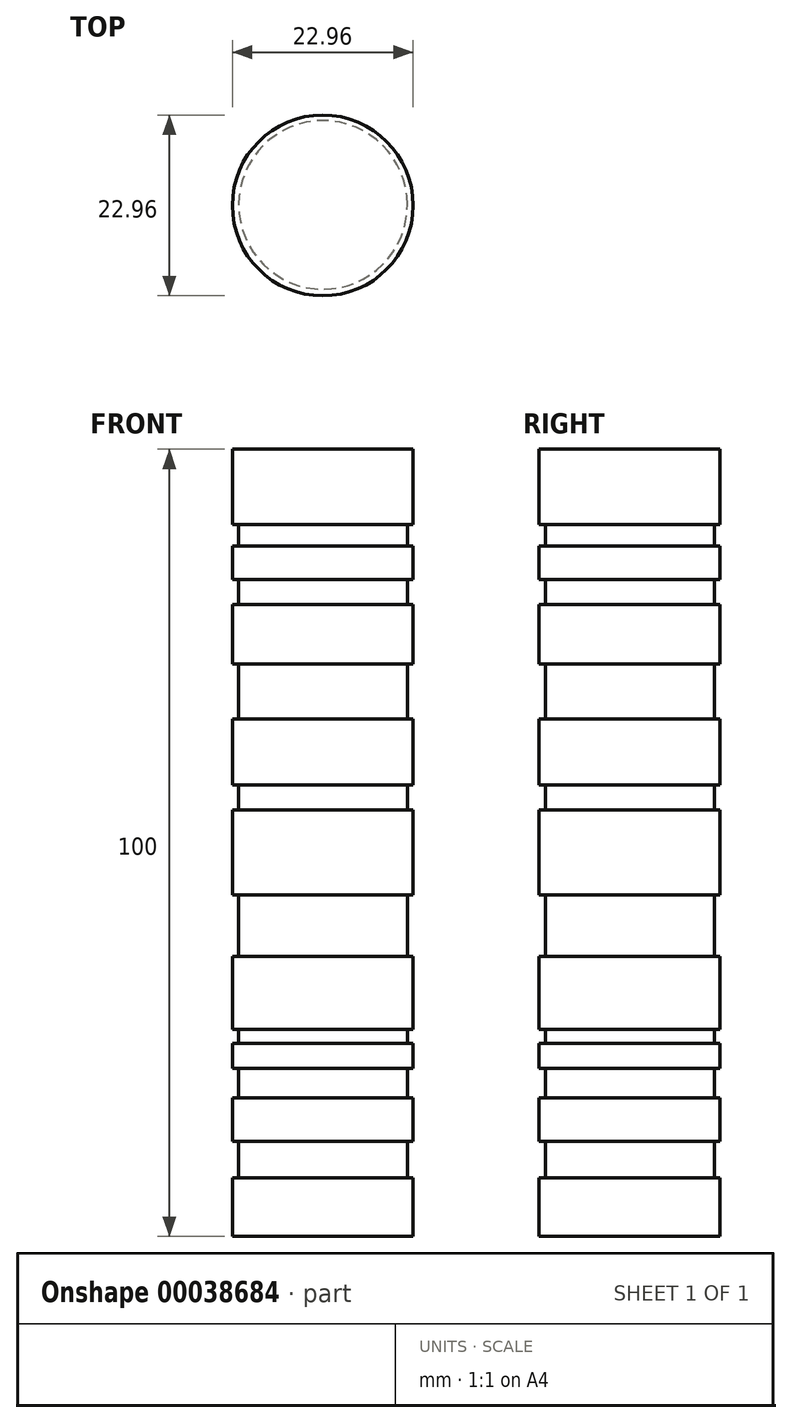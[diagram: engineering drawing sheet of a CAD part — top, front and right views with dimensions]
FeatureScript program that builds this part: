
annotation { "Feature Type Name" : "Feature", "Feature Type Description" : "" }
export const myFeature = defineFeature(function(context is Context, id is Id, definition is map)
    precondition{}
    {
        {
            var Q0;
            Q0=qCreatedBy(makeId("Top.planeOp"),FACE);
            var sketch = newSketch(context, id + "F0", { "sketchPlane" : qUnion([Q0])});
            skCircle(sketch, "E0", {"center": v(-0.04, -0.07) * mm, "radius": 11.48 * mm});
            skCircle(sketch, "E1", {"center": v(0, 0) * mm, "radius": 10.71 * mm});
            skSolve(sketch);
        }
        {
            var Q0;
            Q0=makeQuery(id+"F0.imprint","IMPRINT",FACE,{"disambiguationData":[TD([[makeQuery(id+"F0.imprint","IMPRINT",EDGE,{"derivedFrom":sQuery(id+"F0.wireOp",EDGE,"48e941eb-b95a-4344-8eae-27f2d5f53a51")}),1.0]])]});
            var Q1;
            Q1=makeQuery(id+"F0.imprint","IMPRINT",FACE,{"disambiguationData":[TD([[makeQuery(id+"F0.imprint","IMPRINT",EDGE,{"derivedFrom":sQuery(id+"F0.wireOp",EDGE,"f4a03ec6-5929-497b-a1fc-6486a69c58ac")}),-1.0]])]});
            var Q2;
            Q2=makeQuery(id+"F0.imprint","IMPRINT",FACE,{"disambiguationData":[TD([[makeQuery(id+"F0.imprint","IMPRINT",EDGE,{"derivedFrom":sQuery(id+"F0.wireOp",EDGE,"898b9080-6c66-4597-9512-e4c01d8043e0")}),-1.0]])]});
            var Q3;
            Q3=makeQuery(id+"F0.imprint","IMPRINT",FACE,{"disambiguationData":[TD([[makeQuery(id+"F0.imprint","IMPRINT",EDGE,{"derivedFrom":sQuery(id+"F0.wireOp",EDGE,"E0")}),1.0]])]});
            extrude(context, id + "F1", {"entities" : qUnion([Q0, Q1, Q2, Q3]), "depth" : 100 * mm});
        }
        {
            var Q0;
            Q0=qCreatedBy(makeId("Front.planeOp"),FACE);
            var sketch = newSketch(context, id + "F2", { "sketchPlane" : qUnion([Q0])});
            skLineSegment(sketch, "E2.bottom", {"start": v(-26.5, 12.06) * mm, "end": v(0, 12.06) * mm});
            skLineSegment(sketch, "E2.top", {"start": v(-26.5, 7.42) * mm, "end": v(0, 7.42) * mm});
            skLineSegment(sketch, "E2.left", {"start": v(-26.5, 12.06) * mm, "end": v(-26.5, 7.42) * mm});
            skLineSegment(sketch, "E2.right", {"start": v(0, 12.06) * mm, "end": v(0, 7.42) * mm});
            skLineSegment(sketch, "E3.bottom", {"start": v(-29.9, 26.29) * mm, "end": v(0, 26.29) * mm});
            skLineSegment(sketch, "E3.top", {"start": v(-29.9, 24.55) * mm, "end": v(0, 24.55) * mm});
            skLineSegment(sketch, "E3.left", {"start": v(-29.9, 26.29) * mm, "end": v(-29.9, 24.55) * mm});
            skLineSegment(sketch, "E3.right", {"start": v(0, 26.29) * mm, "end": v(0, 24.55) * mm});
            skLineSegment(sketch, "E4.bottom", {"start": v(-29.9, 43.42) * mm, "end": v(0, 43.42) * mm});
            skLineSegment(sketch, "E4.top", {"start": v(-29.9, 35.58) * mm, "end": v(0, 35.58) * mm});
            skLineSegment(sketch, "E4.left", {"start": v(-29.9, 43.42) * mm, "end": v(-29.9, 35.58) * mm});
            skLineSegment(sketch, "E4.right", {"start": v(0, 43.42) * mm, "end": v(0, 35.58) * mm});
            skPoint(sketch, "E5.oppositeSnap0", {"position": v(0, 39.5) * mm});
            skLineSegment(sketch, "E5.bottom", {"start": v(-32.95, 57.35) * mm, "end": v(0, 57.35) * mm});
            skLineSegment(sketch, "E5.top", {"start": v(-32.95, 54.16) * mm, "end": v(0, 54.16) * mm});
            skLineSegment(sketch, "E5.left", {"start": v(-32.95, 57.35) * mm, "end": v(-32.95, 54.16) * mm});
            skLineSegment(sketch, "E5.right", {"start": v(0, 57.35) * mm, "end": v(0, 54.16) * mm});
            skLineSegment(sketch, "E6.bottom", {"start": v(-32.58, 72.73) * mm, "end": v(0, 72.73) * mm});
            skLineSegment(sketch, "E6.top", {"start": v(-32.58, 65.77) * mm, "end": v(0, 65.77) * mm});
            skLineSegment(sketch, "E6.left", {"start": v(-32.58, 72.73) * mm, "end": v(-32.58, 65.77) * mm});
            skLineSegment(sketch, "E6.right", {"start": v(0, 72.73) * mm, "end": v(0, 65.77) * mm});
            skLineSegment(sketch, "E7.bottom", {"start": v(-32.88, 83.47) * mm, "end": v(0, 83.47) * mm});
            skLineSegment(sketch, "E7.top", {"start": v(-32.88, 80.28) * mm, "end": v(0, 80.28) * mm});
            skLineSegment(sketch, "E7.left", {"start": v(-32.88, 83.47) * mm, "end": v(-32.88, 80.28) * mm});
            skLineSegment(sketch, "E7.right", {"start": v(0, 83.47) * mm, "end": v(0, 80.28) * mm});
            skLineSegment(sketch, "E8.bottom", {"start": v(-32.88, 87.74) * mm, "end": v(0, 87.74) * mm});
            skLineSegment(sketch, "E8.top", {"start": v(-32.88, 90.44) * mm, "end": v(0, 90.44) * mm});
            skLineSegment(sketch, "E8.left", {"start": v(-32.88, 90.44) * mm, "end": v(-32.88, 87.74) * mm});
            skLineSegment(sketch, "E8.right", {"start": v(0, 90.44) * mm, "end": v(0, 87.74) * mm});
            skLineSegment(sketch, "E9", {"start": v(0, 0) * mm, "end": v(0, 99.73) * mm});
            skLineSegment(sketch, "E10.bottom", {"start": v(-27, 21.35) * mm, "end": v(0, 21.35) * mm});
            skLineSegment(sketch, "E10.top", {"start": v(-27, 17.58) * mm, "end": v(0, 17.58) * mm});
            skLineSegment(sketch, "E10.left", {"start": v(-27, 21.35) * mm, "end": v(-27, 17.58) * mm});
            skLineSegment(sketch, "E10.right", {"start": v(0, 21.35) * mm, "end": v(0, 17.58) * mm});
            skSolve(sketch);
        }
        {
            var Q0;
            Q0 = qSketchRegion(id + "F2", true);
            var Q1;
            Q1=sQuery(id+"F2.wireOp",EDGE,"E9");
            revolve(context, id + "F3", {"operationType" : NewBodyOperationType.REMOVE, "entities" : qUnion([Q0]), "axis" : qUnion([Q1]), "revolveType" : RevolveType.FULL, "oppositeDirection" : true});
        }
        {
            var Q0;
            Q0=makeQuery(id+"F0.imprint","IMPRINT",FACE,{"disambiguationData":[TD([[makeQuery(id+"F0.imprint","IMPRINT",EDGE,{"derivedFrom":sQuery(id+"F0.wireOp",EDGE,"E1")}),1.0]])]});
            extrude(context, id + "F4", {"entities" : qUnion([Q0]), "operationType" : NewBodyOperationType.ADD, "depth" : 100 * mm});
        }
    });
